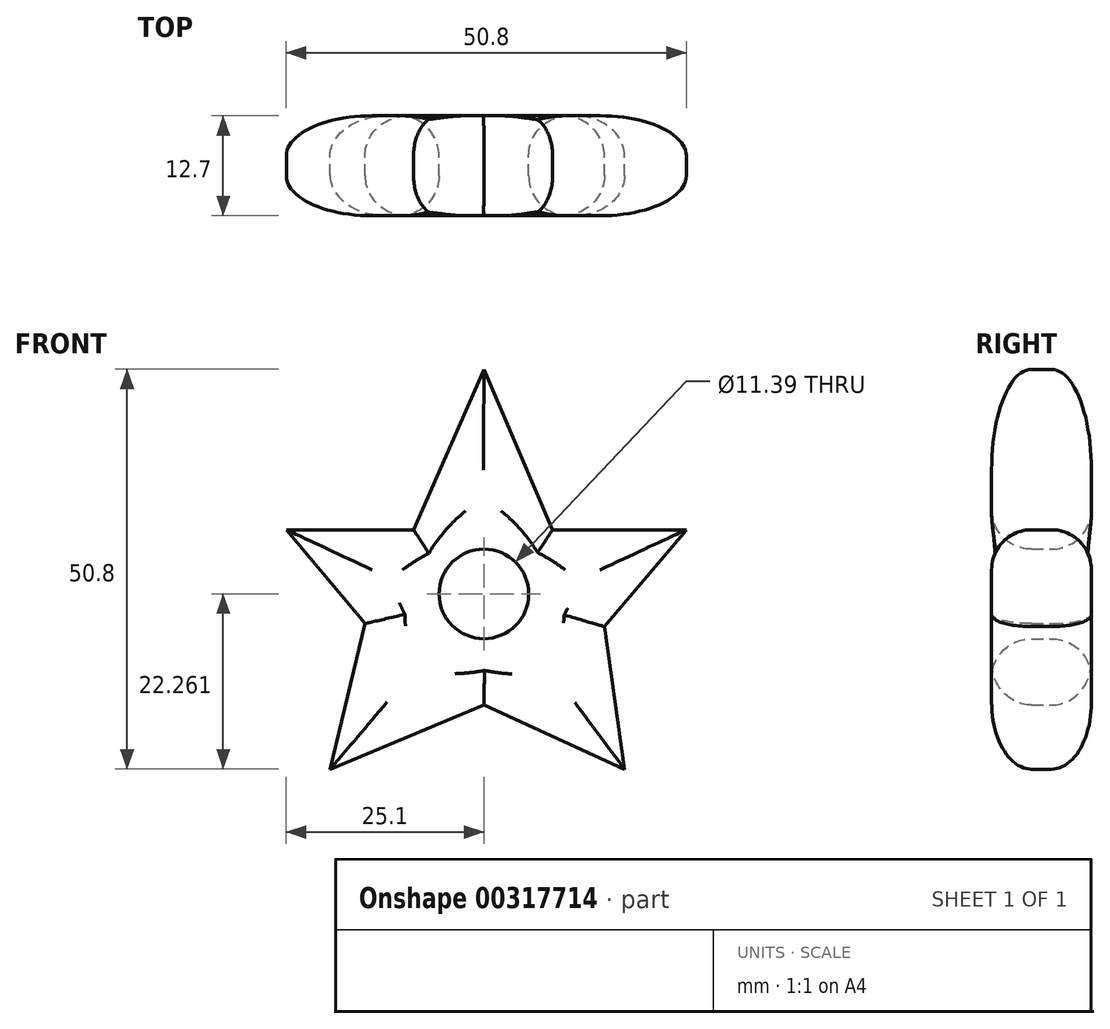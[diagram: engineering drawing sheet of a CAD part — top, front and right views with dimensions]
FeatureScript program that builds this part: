
annotation { "Feature Type Name" : "Feature", "Feature Type Description" : "" }
export const myFeature = defineFeature(function(context is Context, id is Id, definition is map)
    precondition{}
    {
        {
            var Q0;
            Q0=qCreatedBy(makeId("Front.planeOp"),FACE);
            var sketch = newSketch(context, id + "F0", { "sketchPlane" : qUnion([Q0])});
            skLineSegment(sketch, "E0", {"start": v(8.73, 22.27) * mm, "end": v(25.7, 22.27) * mm});
            skLineSegment(sketch, "E1", {"start": v(25.7, 22.27) * mm, "end": v(15.31, 9.97) * mm});
            skLineSegment(sketch, "E2", {"start": v(-8.94, 22.27) * mm, "end": v(-25.1, 22.27) * mm});
            skLineSegment(sketch, "E3", {"start": v(-25.1, 22.27) * mm, "end": v(-15.11, 10.34) * mm});
            skLineSegment(sketch, "E4", {"start": v(-8.94, 22.27) * mm, "end": v(0, 42.66) * mm});
            skLineSegment(sketch, "E5", {"start": v(8.73, 22.27) * mm, "end": v(0, 42.66) * mm});
            skLineSegment(sketch, "E6", {"start": v(-15.11, 10.34) * mm, "end": v(-19.54, -8.14) * mm});
            skLineSegment(sketch, "E7", {"start": v(-19.54, -8.14) * mm, "end": v(0, 0) * mm});
            skLineSegment(sketch, "E8", {"start": v(0, 0) * mm, "end": v(17.87, -8.14) * mm});
            skLineSegment(sketch, "E9", {"start": v(17.87, -8.14) * mm, "end": v(15.31, 9.97) * mm});
            skCircle(sketch, "E10", {"center": v(0, 14.12) * mm, "radius": 5.7 * mm});
            skSolve(sketch);
        }
        {
            var Q0;
            Q0 = qSketchRegion(id + "F0", true);
            extrude(context, id + "F1", {"entities" : qUnion([Q0]), "depth" : 12.7 * mm});
        }
        {
            var Q0;
            Q0=makeQuery(id+"F1.opExtrude","CAP_FACE",FACE,{"disambiguationData":[OSD([sQuery(id+"F0.wireOp",EDGE,"E0"),sQuery(id+"F0.wireOp",EDGE,"E1"),sQuery(id+"F0.wireOp",EDGE,"E2"),sQuery(id+"F0.wireOp",EDGE,"E3"),sQuery(id+"F0.wireOp",EDGE,"E4"),sQuery(id+"F0.wireOp",EDGE,"E5"),sQuery(id+"F0.wireOp",EDGE,"E6"),sQuery(id+"F0.wireOp",EDGE,"E7"),sQuery(id+"F0.wireOp",EDGE,"E8"),sQuery(id+"F0.wireOp",EDGE,"E9"),sQuery(id+"F0.wireOp",EDGE,"E10")])],"isStart":false});
            var Q1;
            Q1=makeQuery(id+"F1.opExtrude","CAP_FACE",FACE,{"disambiguationData":[OSD([sQuery(id+"F0.wireOp",EDGE,"E0"),sQuery(id+"F0.wireOp",EDGE,"E1"),sQuery(id+"F0.wireOp",EDGE,"E2"),sQuery(id+"F0.wireOp",EDGE,"E3"),sQuery(id+"F0.wireOp",EDGE,"E4"),sQuery(id+"F0.wireOp",EDGE,"E5"),sQuery(id+"F0.wireOp",EDGE,"E6"),sQuery(id+"F0.wireOp",EDGE,"E7"),sQuery(id+"F0.wireOp",EDGE,"E8"),sQuery(id+"F0.wireOp",EDGE,"E9"),sQuery(id+"F0.wireOp",EDGE,"E10")])],"isStart":true});
            fillet(context, id + "F2", {"entities" : qUnion([Q0, Q1]), "radius" : 5.08 * mm, "tangentPropagation" : true, "allowEdgeOverflow" : false});
        }
    });
